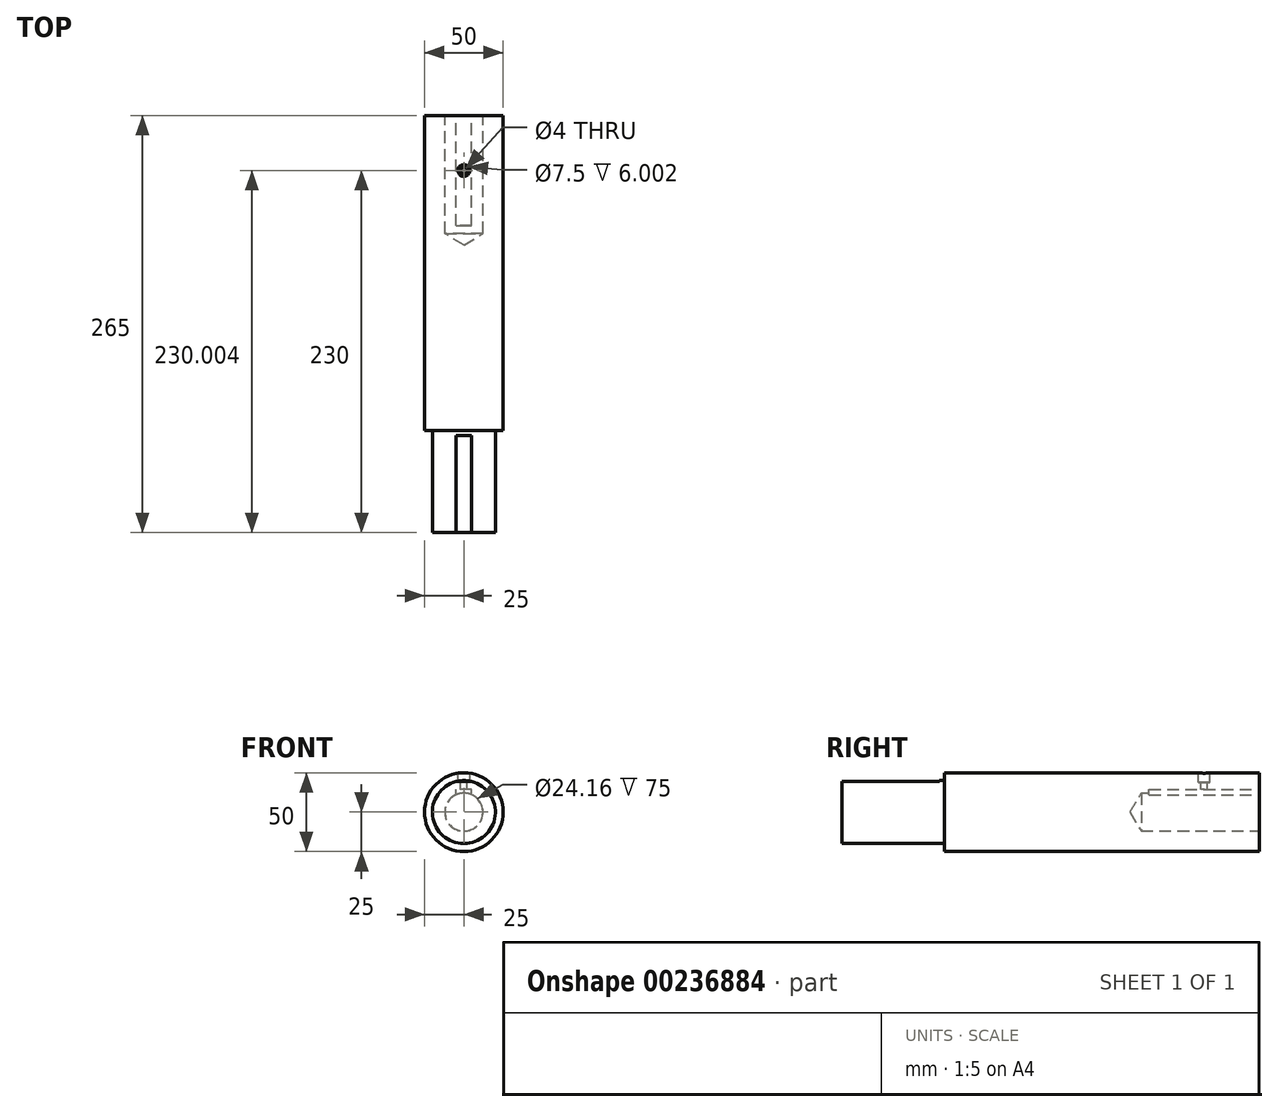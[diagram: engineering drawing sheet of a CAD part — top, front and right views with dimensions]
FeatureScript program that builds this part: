
annotation { "Feature Type Name" : "Feature", "Feature Type Description" : "" }
export const myFeature = defineFeature(function(context is Context, id is Id, definition is map)
    precondition{}
    {
        {
            var Q0;
            Q0=qCreatedBy(makeId("Front.planeOp"),FACE);
            var sketch = newSketch(context, id + "F0", { "sketchPlane" : qUnion([Q0])});
            skCircle(sketch, "E0", {"center": v(0, 0) * mm, "radius": 25 * mm});
            skSolve(sketch);
        }
        {
            var Q0;
            Q0=qSketchRegion(id+"F0",true);
            extrude(context, id + "F1", {"entities" : qUnion([Q0]), "depth" : 200 * mm});
        }
        {
            var Q0;
            Q0=makeQuery(id+"F1.opExtrude","CAP_FACE",FACE,{"disambiguationData":[OSD([sQuery(id+"F0.wireOp",EDGE,"E0")])],"isStart":false});
            var sketch = newSketch(context, id + "F2", { "sketchPlane" : qUnion([Q0])});
            skCircle(sketch, "E1", {"center": v(0, 0) * mm, "radius": 20 * mm});
            skSolve(sketch);
        }
        {
            var Q0;
            Q0=qSketchRegion(id+"F2",true);
            extrude(context, id + "F3", {"entities" : qUnion([Q0]), "operationType" : NewBodyOperationType.ADD, "depth" : 65 * mm});
        }
        {
            var Q0;
            Q0=makeQuery(id+"F3.opExtrude","CAP_FACE",FACE,{"disambiguationData":[OSD([sQuery(id+"F2.wireOp",EDGE,"E1")])],"isStart":false});
            var sketch = newSketch(context, id + "F4", { "sketchPlane" : qUnion([Q0])});
            skLineSegment(sketch, "E2.0", {"start": v(5, 19.36) * mm, "end": v(5, 22.56) * mm});
            skLineSegment(sketch, "E3", {"start": v(5, 19.36) * mm, "end": v(-5, 19.36) * mm});
            skLineSegment(sketch, "E4", {"start": v(-5, 19.36) * mm, "end": v(-5, 22.56) * mm});
            skLineSegment(sketch, "E5", {"start": v(-5, 22.56) * mm, "end": v(5, 22.56) * mm});
            skPoint(sketch, "E6.start.orphan", {"position": v(0, 0) * mm});
            skSolve(sketch);
        }
        {
            var Q0;
            Q0=qSketchRegion(id+"F4",true);
            extrude(context, id + "F5", {"entities" : qUnion([Q0]), "operationType" : NewBodyOperationType.REMOVE, "oppositeDirection" : true, "depth" : 61.7 * mm});
        }
        {
            var Q0;
            Q0=makeQuery(id+"F1.opExtrude","CAP_FACE",FACE,{"disambiguationData":[OSD([sQuery(id+"F0.wireOp",EDGE,"E0")])],"isStart":true});
            var sketch = newSketch(context, id + "F6", { "sketchPlane" : qUnion([Q0])});
            skPoint(sketch, "E7", {"position": v(0, 0) * mm});
            skSolve(sketch);
        }
        {
            var Q0;
            Q0=sQuery(id+"F6.wireOp",VERTEX,"E7");
            var Q1;
            Q1=makeQuery(id+"F1.opExtrude","SWEPT_BODY",BODY,{"disambiguationData":[OSD([sQuery(id+"F0.wireOp",EDGE,"E0")])]});
            hole(context, id + "F7", {"style" : HoleStyle.SIMPLE, "endStyle" : HoleEndStyle.BLIND, "holeDiameter" : 24.16 * mm, "holeDepth" : 75 * mm, "locations" : qUnion([Q0]), "scope" : qUnion([Q1])});
        }
        {
            var Q0;
            Q0=makeQuery(id+"F1.opExtrude","CAP_FACE",FACE,{"disambiguationData":[OSD([sQuery(id+"F0.wireOp",EDGE,"E0")])],"isStart":true});
            var sketch = newSketch(context, id + "F8", { "sketchPlane" : qUnion([Q0])});
            skLineSegment(sketch, "E8.0", {"start": v(-5, 8.84) * mm, "end": v(-5, 14.5) * mm});
            skLineSegment(sketch, "E9.0", {"start": v(5, 8.84) * mm, "end": v(5, 14.5) * mm});
            skLineSegment(sketch, "E10", {"start": v(-5, 14.5) * mm, "end": v(5, 14.5) * mm});
            skLineSegment(sketch, "E11", {"start": v(-5, 8.84) * mm, "end": v(5, 8.84) * mm});
            skPoint(sketch, "E12.orphan", {"position": v(0, 0) * mm});
            skSolve(sketch);
        }
        {
            var Q0;
            Q0=qSketchRegion(id+"F8",true);
            extrude(context, id + "F9", {"entities" : qUnion([Q0]), "operationType" : NewBodyOperationType.REMOVE, "oppositeDirection" : true, "depth" : 70 * mm});
        }
        {
            var Q0;
            Q0=qCreatedBy(makeId("Top.planeOp"),FACE);
            cPlane(context, id + "F10", {"entities" : qUnion([Q0]), "cplaneType" : CPlaneType.OFFSET, "offset" : 25 * mm, "width" : 150 * mm, "height" : 150 * mm});
        }
        {
            var Q0;
            Q0=qCreatedBy(id+"F10.planeOp",FACE);
            var sketch = newSketch(context, id + "F11", { "sketchPlane" : qUnion([Q0])});
            skCircle(sketch, "E13", {"center": v(0, -35) * mm, "radius": 2 * mm});
            skSolve(sketch);
        }
        {
            var Q0;
            Q0=qSketchRegion(id+"F11",true);
            extrude(context, id + "F12", {"entities" : qUnion([Q0]), "operationType" : NewBodyOperationType.REMOVE, "oppositeDirection" : true, "depth" : 25 * mm});
        }
        {
            var Q0;
            Q0=qCreatedBy(id+"F10.planeOp",FACE);
            var sketch = newSketch(context, id + "F13", { "sketchPlane" : qUnion([Q0])});
            skCircle(sketch, "E14", {"center": v(0, -35) * mm, "radius": 3.75 * mm});
            skSolve(sketch);
        }
        {
            var Q0;
            Q0=qSketchRegion(id+"F13",true);
            extrude(context, id + "F14", {"entities" : qUnion([Q0]), "operationType" : NewBodyOperationType.REMOVE, "oppositeDirection" : true, "depth" : 6 * mm});
        }
    });
